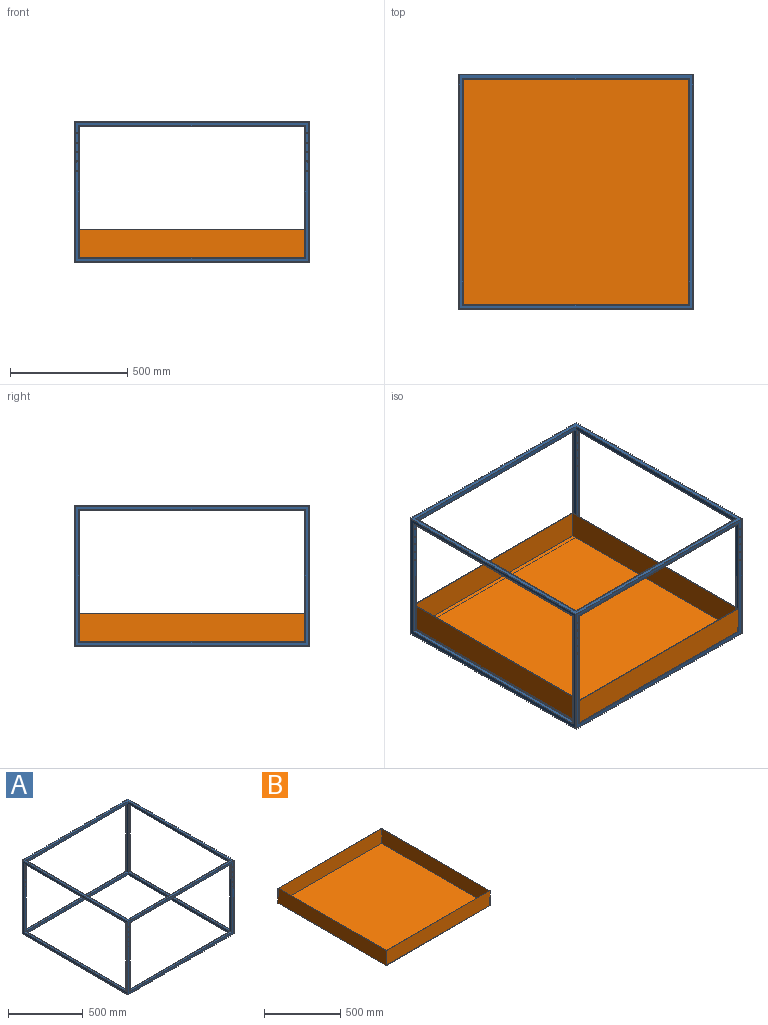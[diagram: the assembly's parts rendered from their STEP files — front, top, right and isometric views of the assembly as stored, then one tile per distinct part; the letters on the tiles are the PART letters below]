
ASSEMBLY  parts=2 mates=1
PART A: 100 faces, bbox 1000x1000x600 mm
  f0: plane 964x16mm, normal (0,0,-1), area 15424mm2, adj f12,f18,f19,f26
  f1: plane 964x16mm, normal (0,0,-1), area 15424mm2, adj f10,f20,f21,f28
  f2: plane 964x16mm, normal (0,0,-1), area 15424mm2, adj f6,f7,f9,f29
  f3: plane 964x16mm, normal (0,0,1), area 15424mm2, adj f12,f18,f19,f25
  f4: plane 964x16mm, normal (0,0,1), area 15424mm2, adj f10,f20,f21,f23
  f5: plane 964x16mm, normal (0,0,1), area 15424mm2, adj f6,f7,f9,f22
  f6: plane 564x16mm, normal (-1,0,0), area 9024mm2, adj f2,f5,f9,f21
  f7: plane 564x16mm, normal (1,0,0), area 9024mm2, adj f2,f5,f9,f18
  f8: plane 996x596mm, normal (0,-1,0), area 49761mm2, adj f10,f11,f12,f13,f14,f15,f16,f17
  f9: plane 996x596mm, normal (0,1,0), area 49761mm2, adj f2,f5,f6,f7,f10,f11,f12,f13
  f10: plane 996x596mm, normal (1,0,0), area 49920mm2, adj f1,f4,f8,f9,f11,f13,f20,f21
  f11: plane 996x996mm, normal (0,0,1), area 62720mm2, adj f8,f9,f10,f12,f26,f27,f28,f29
  f12: plane 996x596mm, normal (-1,0,0), area 49920mm2, adj f0,f3,f8,f9,f11,f13,f18,f19
  f13: plane 996x996mm, normal (0,0,-1), area 62720mm2, adj f8,f9,f10,f12,f22,f23,f24,f25
  f14: plane 564x16mm, normal (-1,0,0), area 9024mm2, adj f8,f15,f17,f20
  f15: plane 964x16mm, normal (0,0,-1), area 15424mm2, adj f8,f14,f16,f27
  f16: plane 564x16mm, normal (1,0,0), area 9024mm2, adj f8,f15,f17,f19
  f17: plane 964x16mm, normal (0,0,1), area 15424mm2, adj f8,f14,f16,f24
  f18: plane 564x16mm, normal (0,-1,0), area 8944.5mm2, adj f0,f3,f7,f12,f45,f46,f47,f48
  f19: plane 564x16mm, normal (0,1,0), area 8944.5mm2, adj f0,f3,f12,f16,f40,f41,f42,f43
  f20: plane 564x16mm, normal (0,1,0), area 8944.5mm2, adj f1,f4,f10,f14,f35,f36,f37,f38
  f21: plane 564x16mm, normal (0,-1,0), area 8944.5mm2, adj f1,f4,f6,f10,f30,f31,f32,f33
  f22: plane 964x16mm, normal (0,-1,0), area 15424mm2, adj f5,f13,f23,f25
  f23: plane 964x16mm, normal (-1,0,0), area 15424mm2, adj f4,f13,f22,f24
  f24: plane 964x16mm, normal (0,1,0), area 15424mm2, adj f13,f17,f23,f25
  f25: plane 964x16mm, normal (1,0,0), area 15424mm2, adj f3,f13,f22,f24
  f26: plane 964x16mm, normal (1,0,0), area 15424mm2, adj f0,f11,f27,f29
  f27: plane 964x16mm, normal (0,1,0), area 15424mm2, adj f11,f15,f26,f28
  f28: plane 964x16mm, normal (-1,0,0), area 15424mm2, adj f1,f11,f27,f29
  f29: plane 964x16mm, normal (0,-1,0), area 15424mm2, adj f2,f11,f26,f28
  f30: cylinder r=2.25mm len=4.5mm, axis (0,-1,0), area 28.3mm2, adj f21,f91
  f31: cylinder r=2.25mm len=4.5mm, axis (0,-1,0), area 28.3mm2, adj f21,f91
  f32: cylinder r=2.25mm len=4.5mm, axis (0,-1,0), area 28.3mm2, adj f21,f91
  f33: cylinder r=2.25mm len=4.5mm, axis (0,-1,0), area 28.3mm2, adj f21,f91
  f34: cylinder r=2.25mm len=4.5mm, axis (0,-1,0), area 28.3mm2, adj f21,f91
  f35: cylinder r=2.25mm len=4.5mm, axis (0,-1,0), area 28.3mm2, adj f20,f90
  f36: cylinder r=2.25mm len=4.5mm, axis (0,-1,0), area 28.3mm2, adj f20,f90
  f37: cylinder r=2.25mm len=4.5mm, axis (0,-1,0), area 28.3mm2, adj f20,f90
  f38: cylinder r=2.25mm len=4.5mm, axis (0,-1,0), area 28.3mm2, adj f20,f90
  f39: cylinder r=2.25mm len=4.5mm, axis (0,-1,0), area 28.3mm2, adj f20,f90
  f40: cylinder r=2.25mm len=4.5mm, axis (0,-1,0), area 28.3mm2, adj f19,f89
  f41: cylinder r=2.25mm len=4.5mm, axis (0,-1,0), area 28.3mm2, adj f19,f89
  f42: cylinder r=2.25mm len=4.5mm, axis (0,-1,0), area 28.3mm2, adj f19,f89
  f43: cylinder r=2.25mm len=4.5mm, axis (0,-1,0), area 28.3mm2, adj f19,f89
  f44: cylinder r=2.25mm len=4.5mm, axis (0,-1,0), area 28.3mm2, adj f19,f89
  f45: cylinder r=2.25mm len=4.5mm, axis (0,-1,0), area 28.3mm2, adj f18,f88
  f46: cylinder r=2.25mm len=4.5mm, axis (0,-1,0), area 28.3mm2, adj f18,f88
  f47: cylinder r=2.25mm len=4.5mm, axis (0,-1,0), area 28.3mm2, adj f18,f88
  f48: cylinder r=2.25mm len=4.5mm, axis (0,-1,0), area 28.3mm2, adj f18,f88
  f49: cylinder r=2.25mm len=4.5mm, axis (0,-1,0), area 28.3mm2, adj f18,f88
  f50: cylinder r=2.25mm len=4.5mm, axis (0,-1,0), area 28.3mm2, adj f9,f79
  f51: cylinder r=2.25mm len=4.5mm, axis (0,-1,0), area 28.3mm2, adj f9,f79
  f52: cylinder r=2.25mm len=4.5mm, axis (0,-1,0), area 28.3mm2, adj f9,f79
  f53: cylinder r=2.25mm len=4.5mm, axis (0,-1,0), area 28.3mm2, adj f9,f79
  f54: cylinder r=2.25mm len=4.5mm, axis (0,-1,0), area 28.3mm2, adj f9,f79
  f55: cylinder r=2.25mm len=4.5mm, axis (0,-1,0), area 28.3mm2, adj f9,f79
  f56: cylinder r=2.25mm len=4.5mm, axis (0,-1,0), area 28.3mm2, adj f9,f79
  f57: cylinder r=2.25mm len=4.5mm, axis (0,-1,0), area 28.3mm2, adj f9,f79
  f58: cylinder r=2.25mm len=4.5mm, axis (0,-1,0), area 28.3mm2, adj f9,f79
  f59: cylinder r=2.25mm len=4.5mm, axis (0,-1,0), area 28.3mm2, adj f9,f79
  f60: cylinder r=2.25mm len=4.5mm, axis (0,-1,0), area 28.3mm2, adj f8,f78
  f61: cylinder r=2.25mm len=4.5mm, axis (0,-1,0), area 28.3mm2, adj f8,f78
  f62: cylinder r=2.25mm len=4.5mm, axis (0,-1,0), area 28.3mm2, adj f8,f78
  f63: cylinder r=2.25mm len=4.5mm, axis (0,-1,0), area 28.3mm2, adj f8,f78
  f64: cylinder r=2.25mm len=4.5mm, axis (0,-1,0), area 28.3mm2, adj f8,f78
  f65: cylinder r=2.25mm len=4.5mm, axis (0,-1,0), area 28.3mm2, adj f8,f78
  f66: cylinder r=2.25mm len=4.5mm, axis (0,-1,0), area 28.3mm2, adj f8,f78
  f67: cylinder r=2.25mm len=4.5mm, axis (0,-1,0), area 28.3mm2, adj f8,f78
  f68: cylinder r=2.25mm len=4.5mm, axis (0,-1,0), area 28.3mm2, adj f8,f78
  f69: cylinder r=2.25mm len=4.5mm, axis (0,-1,0), area 28.3mm2, adj f8,f78
  f70: plane 960x20mm, normal (0,0,1), area 19200mm2, adj f82,f88,f89,f96
  f71: plane 960x20mm, normal (0,0,1), area 19200mm2, adj f80,f90,f91,f98
  f72: plane 960x20mm, normal (0,0,1), area 19200mm2, adj f76,f77,f79,f99
  f73: plane 960x20mm, normal (0,0,-1), area 19200mm2, adj f82,f88,f89,f95
  f74: plane 960x20mm, normal (0,0,-1), area 19200mm2, adj f80,f90,f91,f93
  f75: plane 960x20mm, normal (0,0,-1), area 19200mm2, adj f76,f77,f79,f92
  f76: plane 560x20mm, normal (1,0,0), area 11200mm2, adj f72,f75,f79,f91
  f77: plane 560x20mm, normal (-1,0,0), area 11200mm2, adj f72,f75,f79,f88
  f78: plane 1000x600mm, normal (0,1,0), area 62241mm2, adj f60,f61,f62,f63,f64,f65,f66,f67
  f79: plane 1000x600mm, normal (0,-1,0), area 62241mm2, adj f50,f51,f52,f53,f54,f55,f56,f57
  f80: plane 1000x600mm, normal (-1,0,0), area 62400mm2, adj f71,f74,f78,f79,f81,f83,f90,f91
  f81: plane 1000x1000mm, normal (0,0,-1), area 78400mm2, adj f78,f79,f80,f82,f96,f97,f98,f99
  f82: plane 1000x600mm, normal (1,0,0), area 62400mm2, adj f70,f73,f78,f79,f81,f83,f88,f89
  f83: plane 1000x1000mm, normal (0,0,1), area 78400mm2, adj f78,f79,f80,f82,f92,f93,f94,f95
  f84: plane 560x20mm, normal (1,0,0), area 11200mm2, adj f78,f85,f87,f90
  f85: plane 960x20mm, normal (0,0,1), area 19200mm2, adj f78,f84,f86,f97
  f86: plane 560x20mm, normal (-1,0,0), area 11200mm2, adj f78,f85,f87,f89
  f87: plane 960x20mm, normal (0,0,-1), area 19200mm2, adj f78,f84,f86,f94
  f88: plane 560x20mm, normal (0,1,0), area 11120.5mm2, adj f45,f46,f47,f48,f49,f70,f73,f77
  f89: plane 560x20mm, normal (0,-1,0), area 11120.5mm2, adj f40,f41,f42,f43,f44,f70,f73,f82
  f90: plane 560x20mm, normal (0,-1,0), area 11120.5mm2, adj f35,f36,f37,f38,f39,f71,f74,f80
  f91: plane 560x20mm, normal (0,1,0), area 11120.5mm2, adj f30,f31,f32,f33,f34,f71,f74,f76
  f92: plane 960x20mm, normal (0,1,0), area 19200mm2, adj f75,f83,f93,f95
  f93: plane 960x20mm, normal (1,0,0), area 19200mm2, adj f74,f83,f92,f94
  f94: plane 960x20mm, normal (0,-1,0), area 19200mm2, adj f83,f87,f93,f95
  f95: plane 960x20mm, normal (-1,0,0), area 19200mm2, adj f73,f83,f92,f94
  f96: plane 960x20mm, normal (-1,0,0), area 19200mm2, adj f70,f81,f97,f99
  f97: plane 960x20mm, normal (0,-1,0), area 19200mm2, adj f81,f85,f96,f98
  f98: plane 960x20mm, normal (1,0,0), area 19200mm2, adj f71,f81,f97,f99
  f99: plane 960x20mm, normal (0,1,0), area 19200mm2, adj f72,f81,f96,f98
PART B: 11 faces, bbox 960x1000x120 mm
  f0: plane 960x120mm, normal (0,1,0), area 115200mm2, adj f1,f3,f4,f5
  f1: plane 1000x120mm, normal (-1,0,0), area 120000mm2, adj f0,f2,f3,f4
  f2: plane 960x120mm, normal (0,-1,0), area 115200mm2, adj f1,f3,f4,f5
  f3: plane 1000x960mm, normal (0,0,1), area 9775mm2, adj f0,f1,f2,f5,f6,f7,f8,f10
  f4: plane 1000x960mm, normal (0,0,-1), area 960000mm2, adj f0,f1,f2,f5
  f5: plane 1000x120mm, normal (1,0,0), area 120000mm2, adj f0,f2,f3,f4
  f6: plane 955x117.5mm, normal (0,-1,0), area 112212.5mm2, adj f3,f7,f9,f10
  f7: plane 995x117.5mm, normal (1,0,0), area 116912.5mm2, adj f3,f6,f8,f9
  f8: plane 955x117.5mm, normal (0,1,0), area 112212.5mm2, adj f3,f7,f9,f10
  f9: plane 995x955mm, normal (0,0,1), area 950225mm2, adj f6,f7,f8,f10
  f10: plane 995x117.5mm, normal (-1,0,0), area 116912.5mm2, adj f3,f6,f8,f9
PLACE A t=(-700,500,123)mm
PLACE B t=(-700,500,123)mm
MATE fastened A.f79 <-> B.f2  axis (0,-1,0) through (-220,500,143)mm
